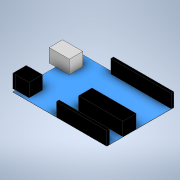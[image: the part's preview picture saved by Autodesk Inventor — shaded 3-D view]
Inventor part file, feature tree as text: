
AUTODESK INVENTOR PART (.ipt)
format: ipt  version: 2020 (Build 240168000, 168)  size: 178,176 bytes
history: native  units: mm
features: extrude x6, sketch x6
ambient origin geometry x8: Origin, YZ Plane, XZ Plane, XY Plane, X Axis, Y Axis, Z Axis, Center Point
bodies: Body1 (feature_tree)
feature tree (12):
  extrude  "Extrusão2"  Depth=50.0mm
  extrude  "Extrusão3"  Depth=45.0mm
  extrude  "Extrusão4"  Depth=37.5mm
  extrude  "Extrusão5"  Depth=10.0mm
  extrude  "Extrusão6"  Depth=10.0mm
  extrude  "Extrusão7"  Depth=10.0mm TaperAngle=0.0deg
  sketch  "Esboço3"  dims[d4=70.0mm d5=50.0mm]
  sketch  "Esboço4"  dims[d6=0.2mm d7=0.0mm d8=45.0mm]
  sketch  "Esboço5"  dims[d9=2.0mm d10=37.5mm]
  sketch  "Esboço7"  dims[d11=2.0mm d12=10.0mm]
  sketch  "Esboço8"  dims[d13=33.0mm d14=10.0mm]
  sketch  "Esboço9"  dims[d15=10.0mm d16=0.0mm d21=10.0mm d22=0.0mm d23=2.0mm d24=0.0mm d25=2.0mm d26=0.0mm d30=10.0mm d31=0.0mm d32=10.0mm d33=10.0mm d34=5.0mm d35=0.0mm]
